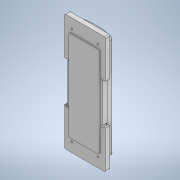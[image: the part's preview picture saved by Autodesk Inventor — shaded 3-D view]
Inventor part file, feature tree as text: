
AUTODESK INVENTOR PART (.ipt)
format: ipt  version: 2021 (Build 250183000, 183)  size: 1,123,840 bytes
history: native  units: mm
features: other x3, sketch x1
ambient origin geometry x8: Origin, YZ Plane, XZ Plane, XY Plane, X Axis, Y Axis, Z Axis, Center Point
bodies: Solid1 (feature_tree)
feature tree (4):
  other  "PanelJigAssembly.iam"
  other  "PanelJig.ipt:1"
  other  "1009799_3D.ipt:2"
  sketch  "Sketch1"  dims[d0=10.0mm]
